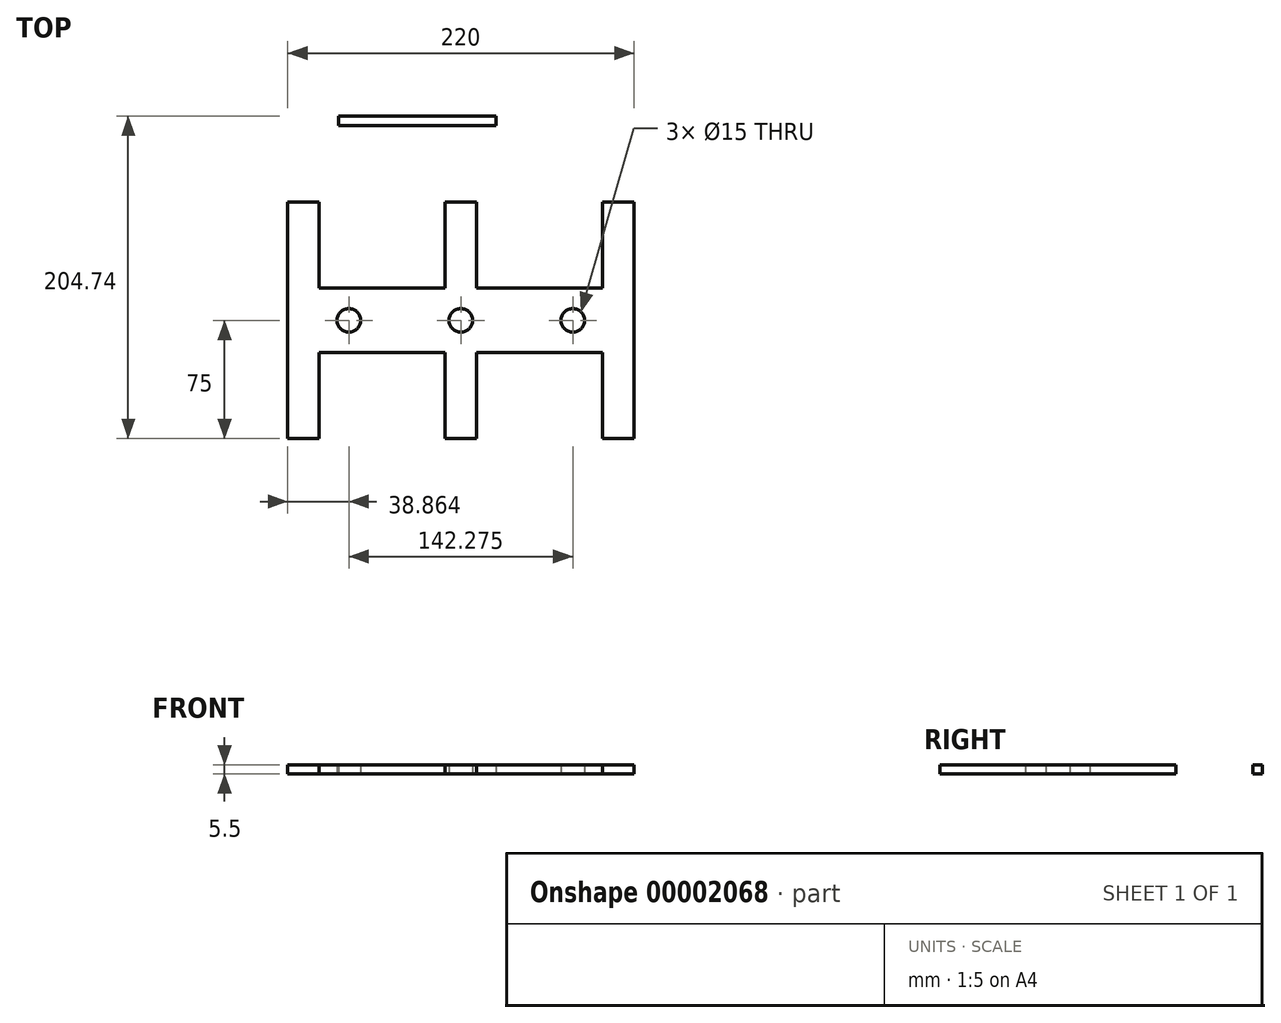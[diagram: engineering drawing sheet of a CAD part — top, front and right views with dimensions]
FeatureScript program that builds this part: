
annotation { "Feature Type Name" : "Feature", "Feature Type Description" : "" }
export const myFeature = defineFeature(function(context is Context, id is Id, definition is map)
    precondition{}
    {
        {
            var Q0;
            Q0=qCreatedBy(makeId("Top.planeOp"),FACE);
            var sketch = newSketch(context, id + "F0", { "sketchPlane" : qUnion([Q0])});
            skLineSegment(sketch, "E0.bottom", {"start": v(-46.71, 54.74) * mm, "end": v(53.29, 54.74) * mm});
            skLineSegment(sketch, "E0.top", {"start": v(-46.71, 48.74) * mm, "end": v(53.29, 48.74) * mm});
            skLineSegment(sketch, "E0.left", {"start": v(-46.71, 54.74) * mm, "end": v(-46.71, 48.74) * mm});
            skLineSegment(sketch, "E0.right", {"start": v(53.29, 54.74) * mm, "end": v(53.29, 48.74) * mm});
            skSolve(sketch);
        }
        {
            var Q0;
            Q0=qCreatedBy(makeId("Top.planeOp"),FACE);
            var sketch = newSketch(context, id + "F1", { "sketchPlane" : qUnion([Q0])});
            skLineSegment(sketch, "E1", {"start": v(-79.03, 0) * mm, "end": v(-59.03, 0) * mm});
            skLineSegment(sketch, "E2", {"start": v(20.97, 0) * mm, "end": v(40.97, 0) * mm});
            skLineSegment(sketch, "E3", {"start": v(120.97, 0) * mm, "end": v(140.97, 0) * mm});
            skLineSegment(sketch, "E4", {"start": v(140.97, 0) * mm, "end": v(140.97, -150) * mm});
            skLineSegment(sketch, "E5", {"start": v(-79.03, 0) * mm, "end": v(-79.03, -150) * mm});
            skLineSegment(sketch, "E6", {"start": v(-59.03, 0) * mm, "end": v(-59.03, -54.51) * mm});
            skLineSegment(sketch, "E7", {"start": v(-59.03, -54.51) * mm, "end": v(20.97, -54.51) * mm});
            skLineSegment(sketch, "E8", {"start": v(20.97, -54.51) * mm, "end": v(20.97, 0) * mm});
            skLineSegment(sketch, "E9", {"start": v(40.97, 0) * mm, "end": v(40.97, -54.51) * mm});
            skLineSegment(sketch, "E10", {"start": v(40.97, -54.51) * mm, "end": v(120.97, -54.51) * mm});
            skLineSegment(sketch, "E11", {"start": v(120.97, -54.51) * mm, "end": v(120.97, 0) * mm});
            skLineSegment(sketch, "E12", {"start": v(-79.03, -150) * mm, "end": v(-59.03, -150) * mm});
            skLineSegment(sketch, "E13", {"start": v(-59.03, -150) * mm, "end": v(-59.03, -95.49) * mm});
            skLineSegment(sketch, "E14", {"start": v(-59.03, -95.49) * mm, "end": v(20.97, -95.49) * mm});
            skLineSegment(sketch, "E15", {"start": v(20.97, -95.49) * mm, "end": v(20.97, -150) * mm});
            skLineSegment(sketch, "E16", {"start": v(20.97, -150) * mm, "end": v(40.97, -150) * mm});
            skLineSegment(sketch, "E17", {"start": v(40.97, -150) * mm, "end": v(40.97, -95.49) * mm});
            skLineSegment(sketch, "E18", {"start": v(40.97, -95.49) * mm, "end": v(120.97, -95.49) * mm});
            skLineSegment(sketch, "E19", {"start": v(120.97, -95.49) * mm, "end": v(120.97, -150) * mm});
            skLineSegment(sketch, "E20", {"start": v(120.97, -150) * mm, "end": v(140.97, -150) * mm});
            skLineSegment(sketch, "E21", {"start": v(-79.03, -75) * mm, "end": v(140.97, -75) * mm, "construction": true});
            skCircle(sketch, "E22", {"center": v(-40.17, -75) * mm, "radius": 7.5 * mm});
            skCircle(sketch, "E23", {"center": v(102.1, -75) * mm, "radius": 7.5 * mm});
            skLineSegment(sketch, "E24", {"start": v(30.97, 0) * mm, "end": v(30.97, -75) * mm, "construction": true});
            skLineSegment(sketch, "E25", {"start": v(30.97, -75) * mm, "end": v(30.97, -150) * mm, "construction": true});
            skCircle(sketch, "E26", {"center": v(30.97, -75) * mm, "radius": 7.5 * mm});
            skSolve(sketch);
        }
        {
            var Q0;
            Q0=makeQuery(id+"F1.imprint","IMPRINT",FACE,{"disambiguationData":[TD([[makeQuery(id+"F1.imprint","IMPRINT",EDGE,{"derivedFrom":sQuery(id+"F1.wireOp",EDGE,"E1")}),-1.0]])]});
            extrude(context, id + "F2", {"entities" : qUnion([Q0]), "depth" : 5.5 * mm});
        }
        {
            var Q0;
            Q0=makeQuery(id+"F0.imprint","IMPRINT",FACE,{"disambiguationData":[TD([[makeQuery(id+"F0.imprint","IMPRINT",EDGE,{"derivedFrom":sQuery(id+"F0.wireOp",EDGE,"E0.bottom")}),-1.0]])]});
            extrude(context, id + "F3", {"entities" : qUnion([Q0]), "depth" : 5.5 * mm});
        }
    });
